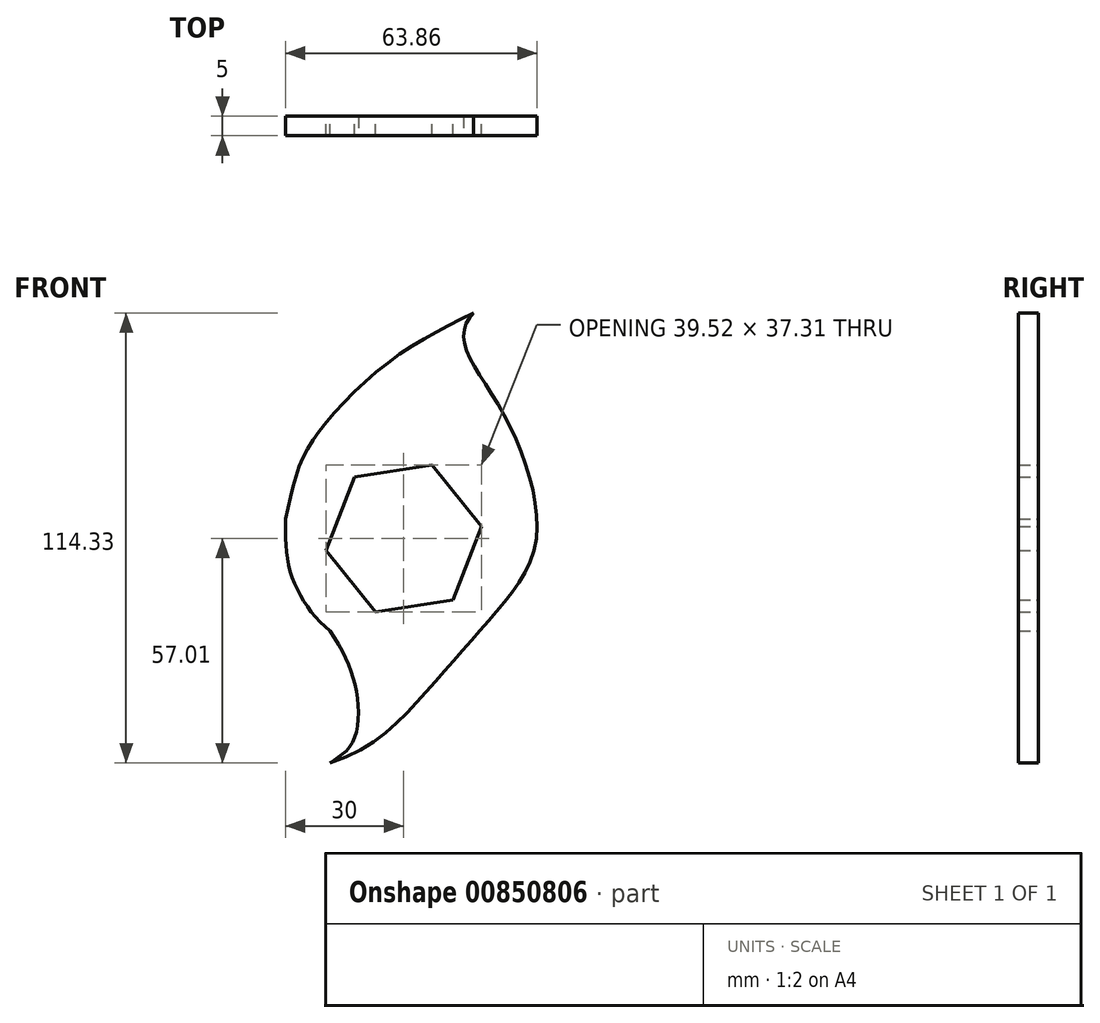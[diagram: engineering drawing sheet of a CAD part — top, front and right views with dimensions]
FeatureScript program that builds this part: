
annotation { "Feature Type Name" : "Feature", "Feature Type Description" : "" }
export const myFeature = defineFeature(function(context is Context, id is Id, definition is map)
    precondition{}
    {
        {
            var Q0;
            Q0=qCreatedBy(makeId("Front.planeOp"),FACE);
            var sketch = newSketch(context, id + "F0", { "sketchPlane" : qUnion([Q0])});
            skLineSegment(sketch, "E0", {"start": v(-60, 0) * mm, "end": v(60, 0) * mm, "construction": true});
            skLineSegment(sketch, "E1", {"start": v(-30, 0) * mm, "end": v(-30, 5) * mm, "construction": true});
            skLineSegment(sketch, "E2", {"start": v(0, -60) * mm, "end": v(0, 65.09) * mm, "construction": true});
            skPoint(sketch, "E3", {"position": v(20, 0) * mm});
            skPoint(sketch, "E4", {"position": v(-20, 0) * mm});
            skFitSpline(sketch, "E5", {"points": [v(17.73, 57.32) * mm, v(15.4, 49.64) * mm, v(25.5, 31.36) * mm, v(33.68, 0) * mm, v(23.97, -18.03) * mm, v(6.93, -37.57) * mm, v(-18.7, -57.01) * mm], "startDerivative": vector(-59.8, -60.42) * mm, "endDerivative": vector(-180.45, -56.72) * mm});
            skFitSpline(sketch, "E6", {"points": [v(-18.7, -57.01) * mm, v(-12.92, -51.66) * mm, v(-12.02, -38.84) * mm, v(-18.7, -23.46) * mm], "startDerivative": vector(26.25, 16.96) * mm, "endDerivative": vector(-27.67, 41.61) * mm});
            skFitSpline(sketch, "E7", {"points": [v(-30, 5) * mm, v(-26.53, 18.24) * mm, v(-20, 29.13) * mm, v(-2.75, 45.6) * mm, v(17.73, 57.32) * mm], "startDerivative": vector(13.44, 63.85) * mm, "endDerivative": vector(72.74, 36) * mm});
            skFitSpline(sketch, "E8", {"points": [v(33.68, 0) * mm, v(29.38, -19.72) * mm, v(21.34, -36.05) * mm, v(5.03, -51.18) * mm, v(-18.7, -57.01) * mm], "startDerivative": vector(-17.02, -154.99) * mm, "endDerivative": vector(-89.2, -12.06) * mm});
            skArc(sketch, "E9.trimOffspring", {"start": v(-30, 0) * mm, "mid": v(-27.03, -13.02) * mm, "end": v(-18.7, -23.46) * mm, "construction": true});
            skArc(sketch, "E10.trimOffspring", {"start": v(-30, 0) * mm, "mid": v(-27.03, -13.02) * mm, "end": v(-18.7, -23.46) * mm});
            skLineSegment(sketch, "E11", {"start": v(-30, 0) * mm, "end": v(-30, 5) * mm});
            skCircle(sketch, "E12.cCircle", {"center": v(0, 0) * mm, "radius": 17.32 * mm, "construction": true});
            skLineSegment(sketch, "E12.0", {"start": v(7.2, 18.66) * mm, "end": v(19.76, 3.09) * mm});
            skLineSegment(sketch, "E12.1", {"start": v(19.76, 3.09) * mm, "end": v(12.55, -15.57) * mm});
            skLineSegment(sketch, "E12.2", {"start": v(12.55, -15.57) * mm, "end": v(-7.2, -18.66) * mm});
            skLineSegment(sketch, "E12.3", {"start": v(-7.2, -18.66) * mm, "end": v(-19.76, -3.09) * mm});
            skLineSegment(sketch, "E12.4", {"start": v(-19.76, -3.09) * mm, "end": v(-12.55, 15.57) * mm});
            skLineSegment(sketch, "E12.5", {"start": v(-12.55, 15.57) * mm, "end": v(7.2, 18.66) * mm});
            skPoint(sketch, "E12.0.midPoint", {"position": v(13.48, 10.87) * mm});
            skSolve(sketch);
        }
        {
            var Q0;
            Q0=makeQuery(id+"F0.imprint","IMPRINT",FACE,{"disambiguationData":[TD([[makeQuery(id+"F0.imprint","IMPRINT",EDGE,{"derivedFrom":sQuery(id+"F0.wireOp",EDGE,"E5")}),-1.0]])]});
            extrude(context, id + "F1", {"entities" : qUnion([Q0]), "depth" : 5 * mm, "offsetDistance" : 25 * mm});
        }
    });
